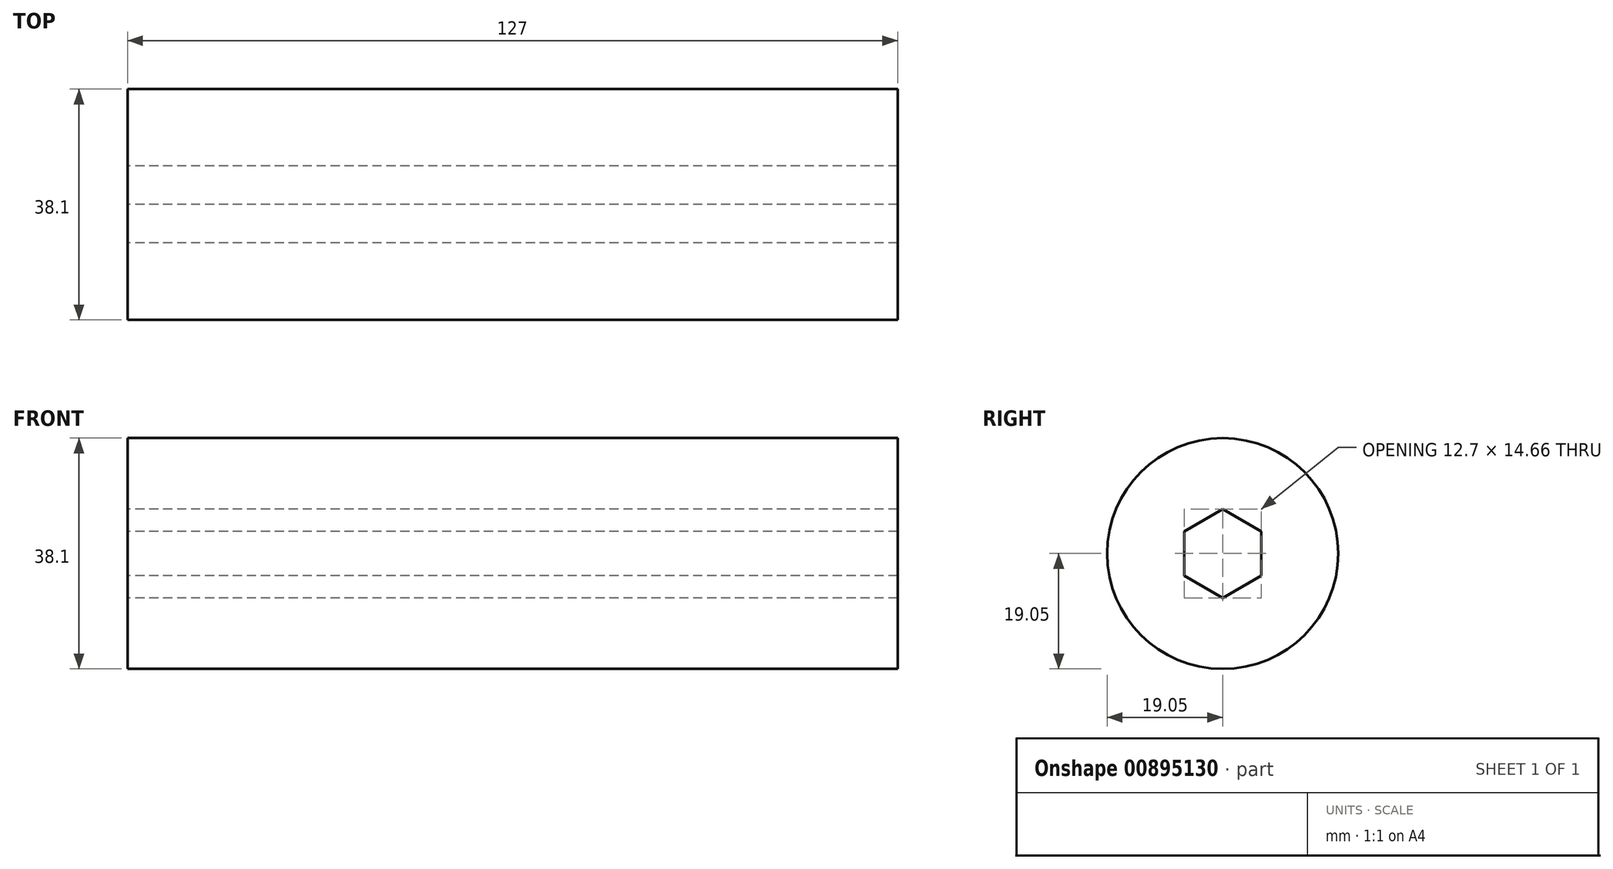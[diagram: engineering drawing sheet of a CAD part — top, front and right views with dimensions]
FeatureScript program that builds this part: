
annotation { "Feature Type Name" : "Feature", "Feature Type Description" : "" }
export const myFeature = defineFeature(function(context is Context, id is Id, definition is map)
    precondition{}
    {
        {
            var Q0;
            Q0=qCreatedBy(makeId("Right.planeOp"),FACE);
            var sketch = newSketch(context, id + "F0", { "sketchPlane" : qUnion([Q0])});
            skCircle(sketch, "E0", {"center": v(0, 0) * mm, "radius": 19.05 * mm});
            skCircle(sketch, "E1.cCircle", {"center": v(0, 0) * mm, "radius": 6.35 * mm, "construction": true});
            skLineSegment(sketch, "E1.0", {"start": v(0, 7.33) * mm, "end": v(6.35, 3.67) * mm});
            skLineSegment(sketch, "E1.1", {"start": v(6.35, 3.67) * mm, "end": v(6.35, -3.67) * mm});
            skLineSegment(sketch, "E1.2", {"start": v(6.35, -3.67) * mm, "end": v(0, -7.33) * mm});
            skLineSegment(sketch, "E1.3", {"start": v(0, -7.33) * mm, "end": v(-6.35, -3.67) * mm});
            skLineSegment(sketch, "E1.4", {"start": v(-6.35, -3.67) * mm, "end": v(-6.35, 3.67) * mm});
            skLineSegment(sketch, "E1.5", {"start": v(-6.35, 3.67) * mm, "end": v(0, 7.33) * mm});
            skPoint(sketch, "E1.0.midPoint", {"position": v(3.17, 5.5) * mm});
            skSolve(sketch);
        }
        {
            var Q0;
            Q0=makeQuery(id+"F0.imprint","IMPRINT",FACE,{"disambiguationData":[TD([[makeQuery(id+"F0.imprint","IMPRINT",EDGE,{"derivedFrom":sQuery(id+"F0.wireOp",EDGE,"E0")}),1.0]])]});
            extrude(context, id + "F1", {"entities" : qUnion([Q0]), "depth" : 127 * mm, "offsetDistance" : 25.4 * mm});
        }
    });
